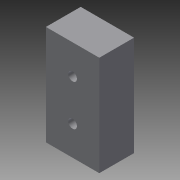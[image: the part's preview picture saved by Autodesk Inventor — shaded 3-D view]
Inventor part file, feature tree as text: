
AUTODESK INVENTOR PART (.ipt)
format: ipt  version: 2015 SP2 (Build 190223200, 223)  size: 92,160 bytes
history: native  units: mm
features: sketch x3, extrude x2, hole x1
ambient origin geometry x8: Origin, YZ Plane, XZ Plane, XY Plane, X Axis, Y Axis, Z Axis, Center Point
bodies: Solid1 (feature_tree)
feature tree (6):
  extrude  "Extrusion1"  Depth=11.499mm
  extrude  "Extrusion2"  Depth=9.499mm
  hole  "Hole1"  [1 undecoded]
  sketch  "Sketch1"  dims[d0=6.14mm d1=11.499mm]
  sketch  "Sketch2"  dims[d2=4.001mm d3=0.0mm d4=9.499mm]
  sketch  "Sketch3"  dims[d5=10.0mm d6=3.001mm d7=0.0mm d8=1.0mm d9=1.0mm d10=6.0mm d11=4.0mm d12=2.0mm d13=90.0deg d14=8.0mm d15=20.594885mm]
note: 1 required parameter value undecoded (feature->parameter linkage not recoverable at this tier; creation-order binding heuristic only, values carry confidence <= 0.55)
